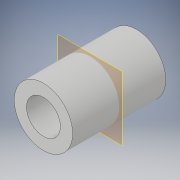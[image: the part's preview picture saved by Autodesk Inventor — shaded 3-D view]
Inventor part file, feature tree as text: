
AUTODESK INVENTOR PART (.ipt)
format: ipt  version: 2018 (Build 220112000, 112)  size: 114,176 bytes
history: native  units: in
note: dims shown in document units (in); Inventor stores cm internally (conversion verified against a paired STEP export)
features: extrude x3, sketch x3, plane x1
ambient origin geometry x8: Origin, YZ Plane, XZ Plane, XY Plane, X Axis, Y Axis, Z Axis, Center Point
bodies: Solid1 (feature_tree)
feature tree (7):
  extrude  "Extrusion1"  Depth=1.0781in
  plane  "Work Plane1"
  extrude  "Extrusion2"  Depth=0.5in TaperAngle=0.0deg
  extrude  "Extrusion3"  Depth=0.5in TaperAngle=0.0deg
  sketch  "Sketch1"  dims[d0=0.625in d1=1.0781in]
  sketch  "Sketch3"  dims[d2=1.7188in d3=0.0in d4=0.5in d5=0.0in]
  sketch  "Sketch5"  dims[d6=0.25in d7=0.5in d8=0.0in]
